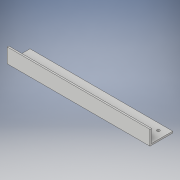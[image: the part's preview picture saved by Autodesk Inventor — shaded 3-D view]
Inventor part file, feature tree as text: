
AUTODESK INVENTOR PART (.ipt)
format: ipt  version: 2018 (Build 220112000, 112)  size: 121,856 bytes
history: native  units: in
note: dims shown in document units (in); Inventor stores cm internally (conversion verified against a paired STEP export)
features: extrude x4, sketch x4
ambient origin geometry x8: Origin, YZ Plane, XZ Plane, XY Plane, X Axis, Y Axis, Z Axis, Center Point
bodies: Solid1 (feature_tree)
feature tree (8):
  extrude  "Extrusion1"  Depth=1.755in
  extrude  "Extrusion2"  Depth=11.0in
  extrude  "Extrusion3"  Depth=1.0in TaperAngle=0.0deg
  extrude  "Extrusion4"  Depth=1.0in
  sketch  "Sketch1"  dims[d0=11.0in d1=1.755in]
  sketch  "Sketch2"  dims[d2=0.125in d3=0.0in d4=11.0in]
  sketch  "Sketch3"  dims[d5=0.125in d6=1.0in d7=0.0in]
  sketch  "Sketch4"  dims[d14=1.0in d15=0.0in d26=0.5in d27=0.2031in d28=1.0in d29=0.0in]
